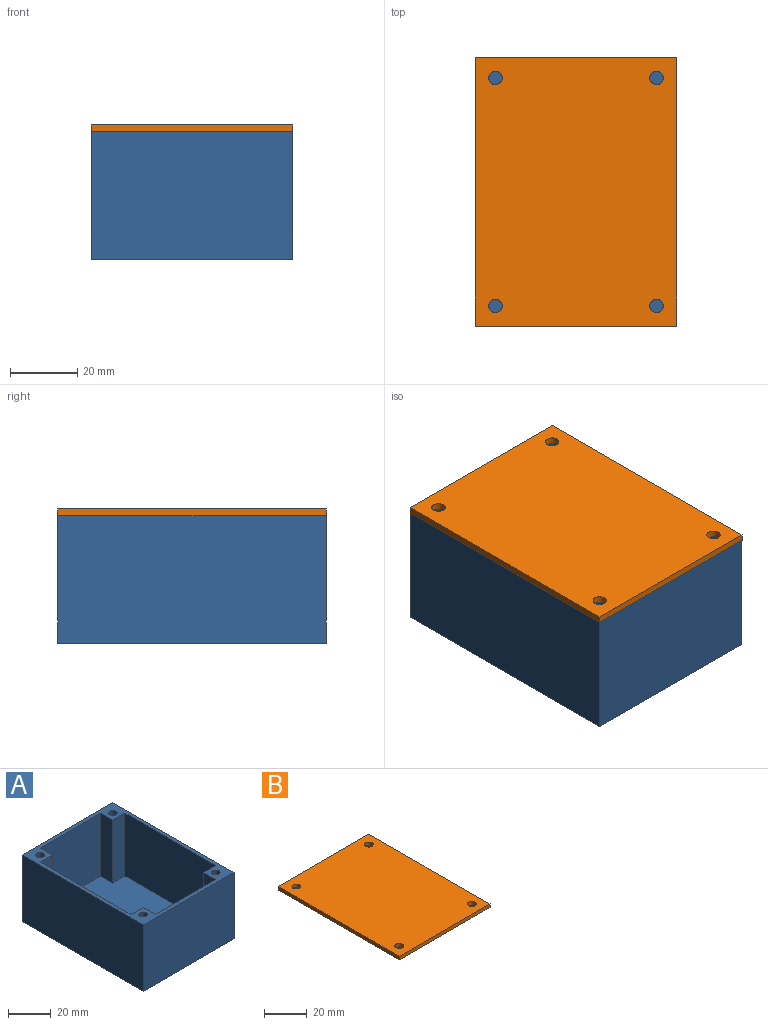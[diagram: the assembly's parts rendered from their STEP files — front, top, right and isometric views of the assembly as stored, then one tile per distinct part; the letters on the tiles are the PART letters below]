
ASSEMBLY  parts=2 mates=1
PART A: 27 faces, bbox 60x80x38 mm
  f0: plane 80x60mm, normal (0,0,1), area 749.7mm2, adj f2,f3,f4,f5,f6,f7,f8,f9
  f1: plane 76x56mm, normal (0,0,1), area 4000mm2, adj f2,f3,f4,f5,f11,f12,f13,f14
  f2: plane 60x36mm, normal (-1,0,0), area 2160mm2, adj f0,f1,f15,f17
  f3: plane 60x36mm, normal (1,0,0), area 2160mm2, adj f0,f1,f12,f13
  f4: plane 40x36mm, normal (0,-1,0), area 1440mm2, adj f0,f1,f14,f16
  f5: plane 40x36mm, normal (0,1,0), area 1440mm2, adj f0,f1,f11,f18
  f6: plane 80x38mm, normal (-1,0,0), area 3040mm2, adj f0,f7,f9,f10
  f7: plane 60x38mm, normal (0,-1,0), area 2280mm2, adj f0,f6,f8,f10
  f8: plane 80x38mm, normal (1,0,0), area 3040mm2, adj f0,f7,f9,f10
  f9: plane 60x38mm, normal (0,1,0), area 2280mm2, adj f0,f6,f8,f10
  f10: plane 80x60mm, normal (0,0,-1), area 4800mm2, adj f6,f7,f8,f9
  f11: plane 36x8mm, normal (1,0,0), area 288mm2, adj f0,f1,f5,f12
  f12: plane 36x8mm, normal (0,1,0), area 288mm2, adj f0,f1,f3,f11
  f13: plane 36x8mm, normal (0,-1,0), area 288mm2, adj f0,f1,f3,f14
  f14: plane 36x8mm, normal (1,0,0), area 288mm2, adj f0,f1,f4,f13
  f15: plane 36x8mm, normal (0,-1,0), area 288mm2, adj f0,f1,f2,f16
  f16: plane 36x8mm, normal (-1,0,0), area 288mm2, adj f0,f1,f4,f15
  f17: plane 36x8mm, normal (0,1,0), area 288mm2, adj f0,f1,f2,f18
  f18: plane 36x8mm, normal (-1,0,0), area 288mm2, adj f0,f1,f5,f17
  f19: cylinder r=2mm len=30mm, axis (0,0,1), area 377mm2, adj f0,f20
  f20: plane 4x4mm, normal (0,0,1), area 12.6mm2, adj f19
  f21: cylinder r=2mm len=30mm, axis (0,0,1), area 377mm2, adj f0,f22
  f22: plane 4x4mm, normal (0,0,1), area 12.6mm2, adj f21
  f23: cylinder r=2mm len=30mm, axis (0,0,1), area 377mm2, adj f0,f24
  f24: plane 4x4mm, normal (0,0,1), area 12.6mm2, adj f23
  f25: cylinder r=2mm len=30mm, axis (0,0,1), area 377mm2, adj f0,f26
  f26: plane 4x4mm, normal (0,0,1), area 12.6mm2, adj f25
PART B: 10 faces, bbox 60x80x2 mm
  f0: plane 80x60mm, normal (0,0,1), area 4749.7mm2, adj f2,f3,f4,f5,f6,f7,f8,f9
  f1: plane 80x60mm, normal (0,0,-1), area 4749.7mm2, adj f2,f3,f4,f5,f6,f7,f8,f9
  f2: plane 60x2mm, normal (0,1,0), area 120mm2, adj f0,f1,f3,f5
  f3: plane 80x2mm, normal (-1,0,0), area 160mm2, adj f0,f1,f2,f4
  f4: plane 60x2mm, normal (0,-1,0), area 120mm2, adj f0,f1,f3,f5
  f5: plane 80x2mm, normal (1,0,0), area 160mm2, adj f0,f1,f2,f4
  f6: cylinder r=2mm len=4mm, axis (0,0,1), area 25.1mm2, adj f0,f1
  f7: cylinder r=2mm len=4mm, axis (0,0,1), area 25.1mm2, adj f0,f1
  f8: cylinder r=2mm len=4mm, axis (0,0,1), area 25.1mm2, adj f0,f1
  f9: cylinder r=2mm len=4mm, axis (0,0,1), area 25.1mm2, adj f0,f1
PLACE A rot(axis=(0,0,-1),0deg) t=(-2.36,2.06,1.39)mm fixed
PLACE B t=(-2.36,102.06,39.39)mm
MATE slider B.f6 <-> A.f25  axis (0,0,-1) through (-26.36,-31.94,39.39)mm
